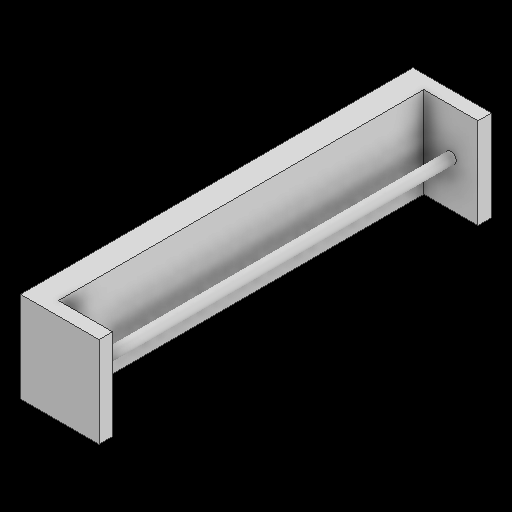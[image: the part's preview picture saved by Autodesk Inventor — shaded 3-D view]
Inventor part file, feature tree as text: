
AUTODESK INVENTOR PART (.ipt)
format: ipt  version: 2025.1 (Build 291241000, 241)  size: 124,928 bytes
history: native  units: in
note: dims shown in document units (in); Inventor stores cm internally (conversion verified against a paired STEP export)
features: extrude x3, sketch x3, projected_geometry x2, other x1
ambient origin geometry x8: Origin, YZ Plane, XZ Plane, XY Plane, X Axis, Y Axis, Z Axis, Center Point
bodies: Body1 (feature_tree)
feature tree (9):
  other  "솔리드1"
  extrude  "돌출1"  Depth=1.1417in
  extrude  "돌출2"  Depth=1.3189in
  extrude  "돌출3"  Depth=5.7087in TaperAngle=0.0deg
  sketch  "스케치1"
  sketch  "스케치2"
  projected_geometry  "투영된 루프1"
  sketch  "스케치3"
  projected_geometry  "투영된 루프2"
